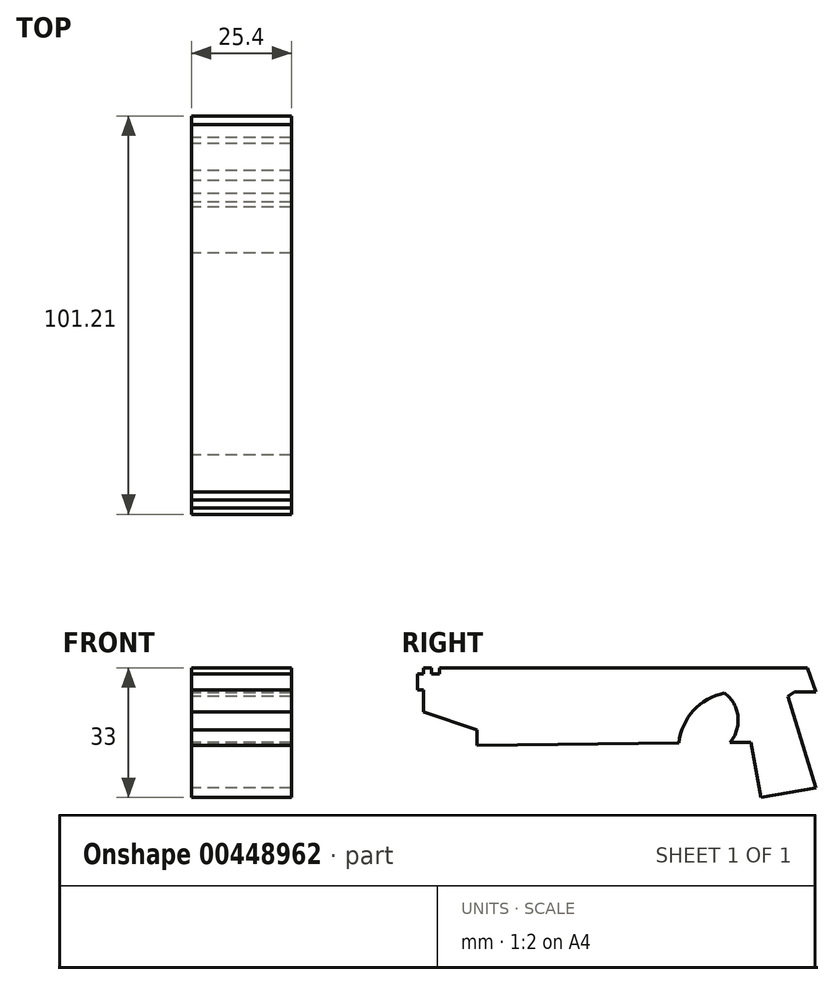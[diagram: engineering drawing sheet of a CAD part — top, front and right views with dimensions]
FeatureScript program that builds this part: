
annotation { "Feature Type Name" : "Feature", "Feature Type Description" : "" }
export const myFeature = defineFeature(function(context is Context, id is Id, definition is map)
    precondition{}
    {
        {
            var Q0;
            Q0=qCreatedBy(makeId("Right.planeOp"),FACE);
            var sketch = newSketch(context, id + "F0", { "sketchPlane" : qUnion([Q0])});
            skLineSegment(sketch, "E0", {"start": v(54.35, 33) * mm, "end": v(-39.1, 33) * mm});
            skLineSegment(sketch, "E1", {"start": v(-39.1, 33) * mm, "end": v(-39.1, 29.26) * mm});
            skLineSegment(sketch, "E2", {"start": v(-39.1, 29.26) * mm, "end": v(-41.12, 29.26) * mm});
            skLineSegment(sketch, "E3", {"start": v(-41.12, 29.26) * mm, "end": v(-41.12, 33) * mm});
            skLineSegment(sketch, "E4", {"start": v(-41.12, 33) * mm, "end": v(-43.13, 33) * mm});
            skLineSegment(sketch, "E5", {"start": v(-43.13, 33) * mm, "end": v(-43.13, 31.41) * mm});
            skLineSegment(sketch, "E6", {"start": v(-43.13, 31.41) * mm, "end": v(-44.71, 31.41) * mm});
            skLineSegment(sketch, "E7", {"start": v(-44.71, 31.41) * mm, "end": v(-44.71, 27.39) * mm});
            skLineSegment(sketch, "E8", {"start": v(-44.71, 27.39) * mm, "end": v(-43.13, 27.39) * mm});
            skLineSegment(sketch, "E9", {"start": v(-43.13, 27.39) * mm, "end": v(-43.13, 31.41) * mm});
            skLineSegment(sketch, "E10", {"start": v(-41.12, 29.26) * mm, "end": v(-43.13, 29.26) * mm});
            skLineSegment(sketch, "E11", {"start": v(-39.1, 31.41) * mm, "end": v(-41.12, 31.41) * mm});
            skLineSegment(sketch, "E12", {"start": v(-43.13, 27.39) * mm, "end": v(-43.13, 21.78) * mm});
            skLineSegment(sketch, "E13", {"start": v(-43.13, 21.78) * mm, "end": v(-29.62, 17.18) * mm});
            skLineSegment(sketch, "E14", {"start": v(-29.62, 17.18) * mm, "end": v(-29.62, 13.3) * mm});
            skLineSegment(sketch, "E15", {"start": v(54.35, 33) * mm, "end": v(56.5, 26.81) * mm});
            skLineSegment(sketch, "E16", {"start": v(56.5, 26.81) * mm, "end": v(51.04, 26.81) * mm});
            skLineSegment(sketch, "E17", {"start": v(51.04, 26.81) * mm, "end": v(49.46, 25.66) * mm});
            skLineSegment(sketch, "E18", {"start": v(49.46, 25.66) * mm, "end": v(56.5, 2.52) * mm});
            skLineSegment(sketch, "E19", {"start": v(56.5, 2.52) * mm, "end": v(42.56, 0) * mm});
            skLineSegment(sketch, "E20", {"start": v(42.56, 0) * mm, "end": v(40.02, 14.04) * mm});
            skLineSegment(sketch, "E21", {"start": v(40.02, 14.04) * mm, "end": v(-29.62, 13.3) * mm});
            skLineSegment(sketch, "E22", {"start": v(40.02, 14.04) * mm, "end": v(36.09, 26.81) * mm});
            skLineSegment(sketch, "E23", {"start": v(36.09, 26.81) * mm, "end": v(51.04, 26.81) * mm});
            skArc(sketch, "E24", {"start": v(36.09, 26.81) * mm, "mid": v(26.4, 23.1) * mm, "end": v(21.72, 13.85) * mm});
            skArc(sketch, "E25", {"start": v(34.65, 13.98) * mm, "mid": v(36.71, 20.55) * mm, "end": v(33.32, 26.55) * mm});
            skLineSegment(sketch, "E26", {"start": v(-29.62, 17.18) * mm, "end": v(4.89, 31.41) * mm});
            skLineSegment(sketch, "E27", {"start": v(4.89, 31.41) * mm, "end": v(52.9, 31.41) * mm});
            skLineSegment(sketch, "E28", {"start": v(52.9, 31.41) * mm, "end": v(52.95, 27.96) * mm});
            skLineSegment(sketch, "E29", {"start": v(52.95, 27.96) * mm, "end": v(36.1, 27.78) * mm});
            skArc(sketch, "E30", {"start": v(36.1, 27.78) * mm, "mid": v(25.65, 23.74) * mm, "end": v(20.41, 13.83) * mm});
            skSolve(sketch);
        }
        {
            var Q0;
            Q0=makeQuery(id+"F0.imprint","IMPRINT",FACE,{"disambiguationData":[TD([[makeQuery(id+"F0.imprint","IMPRINT",EDGE,{"derivedFrom":sQuery(id+"F0.wireOp",EDGE,"E17")}),-1.0]])]});
            var Q1;
            {var subQ0=sQuery(id+"F0.wireOp",EDGE,"E22");Q1=makeQuery(id+"F0.imprint","IMPRINT",FACE,{"disambiguationData":[TD([[makeQuery(id+"F0.imprint","IMPRINT",EDGE,{"derivedFrom":subQ0}),1.0]])]});}
            var Q2;
            {var subQ3=sQuery(id+"F0.wireOp",EDGE,"E0");Q2=makeQuery(id+"F0.imprint","IMPRINT",FACE,{"disambiguationData":[TD([[makeQuery(id+"F0.imprint","IMPRINT",EDGE,{"derivedFrom":subQ3}),1.0]])]});}
            var Q3;
            {var subQ1=sQuery(id+"F0.wireOp",EDGE,"E4");Q3=makeQuery(id+"F0.imprint","IMPRINT",FACE,{"disambiguationData":[TD([[makeQuery(id+"F0.imprint","IMPRINT",EDGE,{"derivedFrom":subQ1}),1.0]])]});}
            var Q4;
            {var subQ0=sQuery(id+"F0.wireOp",EDGE,"E2");Q4=makeQuery(id+"F0.imprint","IMPRINT",FACE,{"disambiguationData":[TD([[makeQuery(id+"F0.imprint","IMPRINT",EDGE,{"derivedFrom":subQ0}),-1.0]])]});}
            var Q5;
            {var subQ3=sQuery(id+"F0.wireOp",EDGE,"E6");Q5=makeQuery(id+"F0.imprint","IMPRINT",FACE,{"disambiguationData":[TD([[makeQuery(id+"F0.imprint","IMPRINT",EDGE,{"derivedFrom":subQ3}),1.0]])]});}
            var Q6;
            {var subQ1=sQuery(id+"F0.wireOp",EDGE,"E14");Q6=makeQuery(id+"F0.imprint","IMPRINT",FACE,{"disambiguationData":[TD([[makeQuery(id+"F0.imprint","IMPRINT",EDGE,{"derivedFrom":subQ1}),1.0]])]});}
            extrude(context, id + "F1", {"entities" : qUnion([Q0, Q1, Q2, Q3, Q4, Q5, Q6]), "depth" : 25.4 * mm});
        }
    });
